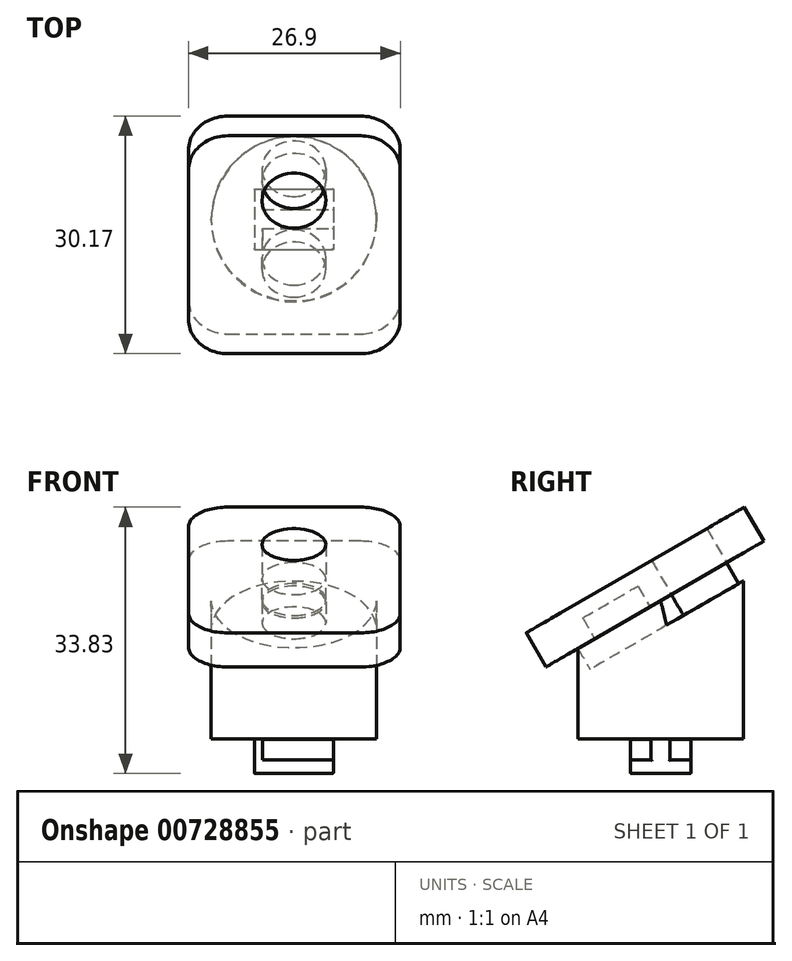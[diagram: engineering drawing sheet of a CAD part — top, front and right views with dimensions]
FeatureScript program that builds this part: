
annotation { "Feature Type Name" : "Feature", "Feature Type Description" : "" }
export const myFeature = defineFeature(function(context is Context, id is Id, definition is map)
    precondition{}
    {
        {
            var Q0;
            Q0=qCreatedBy(makeId("Top.planeOp"),FACE);
            var sketch = newSketch(context, id + "F0", { "sketchPlane" : qUnion([Q0])});
            skLineSegment(sketch, "E0.bottom", {"start": v(-34.1, 11.14) * mm, "end": v(-24.1, 11.14) * mm});
            skLineSegment(sketch, "E0.top", {"start": v(-34.1, 3.44) * mm, "end": v(-24.1, 3.44) * mm});
            skLineSegment(sketch, "E0.left", {"start": v(-34.1, 11.14) * mm, "end": v(-34.1, 3.44) * mm});
            skLineSegment(sketch, "E0.right", {"start": v(-24.1, 11.14) * mm, "end": v(-24.1, 3.44) * mm});
            skLineSegment(sketch, "E1", {"start": v(-38.76, 7.29) * mm, "end": v(-19.78, 7.29) * mm, "construction": true});
            skPoint(sketch, "E1.startSnap0", {"position": v(-34.1, 7.29) * mm});
            skLineSegment(sketch, "E2", {"start": v(-34.1, 6.09) * mm, "end": v(-24.1, 6.09) * mm});
            skLineSegment(sketch, "E3", {"start": v(-33.1, 11.14) * mm, "end": v(-33.1, 3.44) * mm});
            skLineSegment(sketch, "E4.MirrorCS", {"start": v(-34.1, 8.49) * mm, "end": v(-24.1, 8.49) * mm});
            skLineSegment(sketch, "E5", {"start": v(-29.1, 14.12) * mm, "end": v(-29.1, 1.6) * mm, "construction": true});
            skPoint(sketch, "E5.startSnap0", {"position": v(-29.1, 11.14) * mm});
            skCircle(sketch, "E6", {"center": v(-29.1, 7.29) * mm, "radius": 10.5 * mm});
            skSolve(sketch);
        }
        {
            var Q0;
            {var subQ0=sQuery(id+"F0.wireOp",EDGE,"E0.left");var subQ1=sQuery(id+"F0.wireOp",EDGE,"E0.bottom");var subQ2=makeQuery(id+"F0.imprint","INTERSECT",VERTEX,{"derivedFrom":[subQ1,subQ0]});Q0=makeQuery(id+"F0.imprint","IMPRINT",FACE,{"disambiguationData":[TD([[makeQuery(id+"F0.imprint","IMPRINT",EDGE,{"disambiguationData":[TD([[subQ2,-1.0]])],"derivedFrom":subQ1}),-1.0]])]});}
            var Q1;
            {var subQ0=sQuery(id+"F0.wireOp",EDGE,"E2");var subQ1=sQuery(id+"F0.wireOp",EDGE,"E0.left");var subQ2=makeQuery(id+"F0.imprint","INTERSECT",VERTEX,{"derivedFrom":[subQ1,subQ0]});Q1=makeQuery(id+"F0.imprint","IMPRINT",FACE,{"disambiguationData":[TD([[makeQuery(id+"F0.imprint","IMPRINT",EDGE,{"disambiguationData":[TD([[subQ2,1.0]])],"derivedFrom":subQ1}),1.0]])]});}
            var Q2;
            {var subQ0=sQuery(id+"F0.wireOp",EDGE,"E0.right");var subQ1=sQuery(id+"F0.wireOp",EDGE,"E0.bottom");var subQ2=makeQuery(id+"F0.imprint","INTERSECT",VERTEX,{"derivedFrom":[subQ1,subQ0]});Q2=makeQuery(id+"F0.imprint","IMPRINT",FACE,{"disambiguationData":[TD([[makeQuery(id+"F0.imprint","IMPRINT",EDGE,{"disambiguationData":[TD([[subQ2,1.0]])],"derivedFrom":subQ1}),-1.0]])]});}
            var Q3;
            {var subQ0=sQuery(id+"F0.wireOp",EDGE,"E2");var subQ1=sQuery(id+"F0.wireOp",EDGE,"E0.right");var subQ2=makeQuery(id+"F0.imprint","INTERSECT",VERTEX,{"derivedFrom":[subQ1,subQ0]});Q3=makeQuery(id+"F0.imprint","IMPRINT",FACE,{"disambiguationData":[TD([[makeQuery(id+"F0.imprint","IMPRINT",EDGE,{"disambiguationData":[TD([[subQ2,1.0]])],"derivedFrom":subQ1}),-1.0]])]});}
            var Q4;
            {var subQ0=sQuery(id+"F0.wireOp",EDGE,"E0.right");var subQ1=sQuery(id+"F0.wireOp",EDGE,"E0.top");var subQ2=makeQuery(id+"F0.imprint","INTERSECT",VERTEX,{"derivedFrom":[subQ1,subQ0]});Q4=makeQuery(id+"F0.imprint","IMPRINT",FACE,{"disambiguationData":[TD([[makeQuery(id+"F0.imprint","IMPRINT",EDGE,{"disambiguationData":[TD([[subQ2,1.0]])],"derivedFrom":subQ1}),1.0]])]});}
            var Q5;
            {var subQ0=sQuery(id+"F0.wireOp",EDGE,"E0.left");var subQ1=sQuery(id+"F0.wireOp",EDGE,"E0.top");var subQ2=makeQuery(id+"F0.imprint","INTERSECT",VERTEX,{"derivedFrom":[subQ1,subQ0]});Q5=makeQuery(id+"F0.imprint","IMPRINT",FACE,{"disambiguationData":[TD([[makeQuery(id+"F0.imprint","IMPRINT",EDGE,{"disambiguationData":[TD([[subQ2,-1.0]])],"derivedFrom":subQ1}),1.0]])]});}
            extrude(context, id + "F1", {"entities" : qUnion([Q0, Q1, Q2, Q3, Q4, Q5]), "depth" : 1.7 * mm, "offsetDistance" : 25 * mm});
        }
        {
            var Q0;
            {var subQ0=sQuery(id+"F0.wireOp",EDGE,"E2");var subQ1=sQuery(id+"F0.wireOp",EDGE,"E0.right");var subQ2=makeQuery(id+"F0.imprint","INTERSECT",VERTEX,{"derivedFrom":[subQ1,subQ0]});Q0=makeQuery(id+"F0.imprint","IMPRINT",FACE,{"disambiguationData":[TD([[makeQuery(id+"F0.imprint","IMPRINT",EDGE,{"disambiguationData":[TD([[subQ2,1.0]])],"derivedFrom":subQ1}),-1.0]])]});}
            extrude(context, id + "F2", {"entities" : qUnion([Q0]), "operationType" : NewBodyOperationType.ADD, "oppositeDirection" : true, "depth" : (2.6 + 1.7) * mm, "offsetDistance" : 25 * mm});
        }
        {
            var Q0;
            Q0=makeQuery(id+"F1.opExtrude","CAP_FACE",FACE,{"disambiguationData":[OSD([sQuery(id+"F0.wireOp",EDGE,"E0.bottom"),sQuery(id+"F0.wireOp",EDGE,"E0.top"),sQuery(id+"F0.wireOp",EDGE,"E0.left"),sQuery(id+"F0.wireOp",EDGE,"E0.right")])],"isStart":true});
            extrude(context, id + "F3", {"entities" : qUnion([Q0]), "operationType" : NewBodyOperationType.ADD, "depth" : (2.6 + 1.7) * mm, "offsetDistance" : 25 * mm, "hasSecondDirection" : true, "secondDirectionOppositeDirection" : false, "secondDirectionDepth" : 2.6 * mm});
        }
        {
            var Q0;
            {var subQ0=sQuery(id+"F0.wireOp",EDGE,"E0.left");var subQ1=sQuery(id+"F0.wireOp",EDGE,"E0.bottom");var subQ2=makeQuery(id+"F0.imprint","INTERSECT",VERTEX,{"derivedFrom":[subQ1,subQ0]});Q0=makeQuery(id+"F0.imprint","IMPRINT",FACE,{"disambiguationData":[TD([[makeQuery(id+"F0.imprint","IMPRINT",EDGE,{"disambiguationData":[TD([[subQ2,-1.0]])],"derivedFrom":subQ1}),-1.0]])]});}
            var Q1;
            {var subQ0=sQuery(id+"F0.wireOp",EDGE,"E2");var subQ1=sQuery(id+"F0.wireOp",EDGE,"E0.left");var subQ2=makeQuery(id+"F0.imprint","INTERSECT",VERTEX,{"derivedFrom":[subQ1,subQ0]});Q1=makeQuery(id+"F0.imprint","IMPRINT",FACE,{"disambiguationData":[TD([[makeQuery(id+"F0.imprint","IMPRINT",EDGE,{"disambiguationData":[TD([[subQ2,1.0]])],"derivedFrom":subQ1}),1.0]])]});}
            var Q2;
            {var subQ0=sQuery(id+"F0.wireOp",EDGE,"E0.left");var subQ1=sQuery(id+"F0.wireOp",EDGE,"E0.top");var subQ2=makeQuery(id+"F0.imprint","INTERSECT",VERTEX,{"derivedFrom":[subQ1,subQ0]});Q2=makeQuery(id+"F0.imprint","IMPRINT",FACE,{"disambiguationData":[TD([[makeQuery(id+"F0.imprint","IMPRINT",EDGE,{"disambiguationData":[TD([[subQ2,-1.0]])],"derivedFrom":subQ1}),1.0]])]});}
            var Q3;
            Q3=makeQuery(id+"F3.opExtrude","CAP_FACE",FACE,{"disambiguationData":[OSD([sQuery(id+"F0.wireOp",EDGE,"E0.bottom"),sQuery(id+"F0.wireOp",EDGE,"E0.top"),sQuery(id+"F0.wireOp",EDGE,"E0.left"),sQuery(id+"F0.wireOp",EDGE,"E0.right")])],"isStart":true});
            extrude(context, id + "F4", {"entities" : qUnion([Q0, Q1, Q2]), "operationType" : NewBodyOperationType.ADD, "endBound" : BoundingType.UP_TO_SURFACE, "oppositeDirection" : true, "depth" : 25 * mm, "endBoundEntityFace" : qUnion([Q3]), "offsetDistance" : 25 * mm});
        }
        {
            var Q0;
            Q0=makeQuery(id+"F0.imprint","IMPRINT",FACE,{"disambiguationData":[TD([[makeQuery(id+"F0.imprint","IMPRINT",EDGE,{"derivedFrom":sQuery(id+"F0.wireOp",EDGE,"E6")}),1.0]])]});
            extrude(context, id + "F5", {"entities" : qUnion([Q0]), "operationType" : NewBodyOperationType.ADD, "depth" : 1.7 * mm, "offsetDistance" : 25 * mm, "hasSecondDirection" : true, "secondDirectionOppositeDirection" : false, "secondDirectionDepth" : .1 * mm});
        }
        {
            var Q0;
            {var subQ0=sQuery(id+"F0.wireOp",EDGE,"E0.right");var subQ1=sQuery(id+"F0.wireOp",EDGE,"E0.top");Q0=makeQuery(id+"F2.boolean.opBoolean","SPLIT",EDGE,{"disambiguationData":[TD([makeQuery(id+"F1.opExtrude","SWEPT_FACE",FACE,{"disambiguationData":[OSD([subQ1])]})])],"derivedFrom":makeQuery(id+"F1.opExtrude","CAP_EDGE",EDGE,{"disambiguationData":[OSD([subQ0])],"isStart":true})});}
            var Q1;
            {var subQ0=sQuery(id+"F0.wireOp",EDGE,"E0.right");var subQ1=sQuery(id+"F0.wireOp",EDGE,"E0.bottom");Q1=makeQuery(id+"F2.boolean.opBoolean","SPLIT",EDGE,{"disambiguationData":[TD([makeQuery(id+"F1.opExtrude","SWEPT_FACE",FACE,{"disambiguationData":[OSD([subQ1])]})])],"derivedFrom":makeQuery(id+"F1.opExtrude","CAP_EDGE",EDGE,{"disambiguationData":[OSD([subQ0])],"isStart":true})});}
            var Q2;
            Q2=makeQuery(id+"F2.opExtrude","SWEPT_EDGE",EDGE,{"disambiguationData":[OSD([sQuery(id+"F0.wireOp",EDGE,"E0.right"),sQuery(id+"F0.wireOp",EDGE,"E2")])]});
            var Q3;
            Q3=makeQuery(id+"F2.opExtrude","SWEPT_EDGE",EDGE,{"disambiguationData":[OSD([sQuery(id+"F0.wireOp",EDGE,"E0.right"),sQuery(id+"F0.wireOp",EDGE,"E4.MirrorCS")])]});
            var Q4;
            {var subQ0=sQuery(id+"F0.wireOp",EDGE,"E0.right");var subQ1=sQuery(id+"F0.wireOp",EDGE,"E0.bottom");Q4=makeQuery(id+"F3.opExtrude","CAP_EDGE",EDGE,{"disambiguationData":[OSD([subQ0]),TDD([makeQuery(id+"F2.boolean.opBoolean","SPLIT",EDGE,{"disambiguationData":[TD([makeQuery(id+"F1.opExtrude","SWEPT_FACE",FACE,{"disambiguationData":[OSD([subQ1])]})])],"derivedFrom":makeQuery(id+"F1.opExtrude","CAP_EDGE",EDGE,{"disambiguationData":[OSD([subQ0])],"isStart":true})})])],"isStart":true});}
            var Q5;
            {var subQ0=sQuery(id+"F0.wireOp",EDGE,"E0.right");var subQ1=sQuery(id+"F0.wireOp",EDGE,"E0.top");Q5=makeQuery(id+"F3.opExtrude","CAP_EDGE",EDGE,{"disambiguationData":[OSD([subQ0]),TDD([makeQuery(id+"F2.boolean.opBoolean","SPLIT",EDGE,{"disambiguationData":[TD([makeQuery(id+"F1.opExtrude","SWEPT_FACE",FACE,{"disambiguationData":[OSD([subQ1])]})])],"derivedFrom":makeQuery(id+"F1.opExtrude","CAP_EDGE",EDGE,{"disambiguationData":[OSD([subQ0])],"isStart":true})})])],"isStart":true});}
            var Q6;
            Q6=makeQuery(id+"F3.opExtrude","SWEPT_EDGE",EDGE,{"disambiguationData":[OSD([sQuery(id+"F0.wireOp",EDGE,"E0.top"),sQuery(id+"F0.wireOp",EDGE,"E0.right")])]});
            var Q7;
            {var subQ0=sQuery(id+"F0.wireOp",EDGE,"E0.right");var subQ2=sQuery(id+"F0.wireOp",EDGE,"E0.top");var subQ4=sQuery(id+"F0.wireOp",EDGE,"E0.bottom");var subQ6=makeQuery(id+"F1.opExtrude","CAP_EDGE",EDGE,{"disambiguationData":[OSD([subQ0])],"isStart":true});Q7=makeQuery(id+"F3.boolean.opBoolean","MERGE",EDGE,{"derivedFrom":[makeQuery(id+"F2.opExtrude","CAP_EDGE",EDGE,{"disambiguationData":[OSD([subQ0])],"isStart":false}),makeQuery(id+"F3.opExtrude","CAP_EDGE",EDGE,{"disambiguationData":[OSD([subQ0]),TDD([makeQuery(id+"F2.boolean.opBoolean","SPLIT",EDGE,{"disambiguationData":[TD([makeQuery(id+"F1.opExtrude","SWEPT_FACE",FACE,{"disambiguationData":[OSD([subQ4])]})])],"derivedFrom":subQ6})])],"isStart":false}),makeQuery(id+"F3.opExtrude","CAP_EDGE",EDGE,{"disambiguationData":[OSD([subQ0]),TDD([makeQuery(id+"F2.boolean.opBoolean","SPLIT",EDGE,{"disambiguationData":[TD([makeQuery(id+"F1.opExtrude","SWEPT_FACE",FACE,{"disambiguationData":[OSD([subQ2])]})])],"derivedFrom":subQ6})])],"isStart":false})]});}
            var Q8;
            Q8=makeQuery(id+"F3.opExtrude","SWEPT_EDGE",EDGE,{"disambiguationData":[OSD([sQuery(id+"F0.wireOp",EDGE,"E0.bottom"),sQuery(id+"F0.wireOp",EDGE,"E0.right")])]});
            var Q9;
            Q9=makeQuery(id+"F1.opExtrude","CAP_EDGE",EDGE,{"disambiguationData":[OSD([sQuery(id+"F0.wireOp",EDGE,"E0.top")])],"isStart":true});
            var Q10;
            Q10=makeQuery(id+"F1.opExtrude","CAP_EDGE",EDGE,{"disambiguationData":[OSD([sQuery(id+"F0.wireOp",EDGE,"E0.bottom")])],"isStart":true});
            var Q11;
            Q11=makeQuery(id+"F3.opExtrude","CAP_EDGE",EDGE,{"disambiguationData":[OSD([sQuery(id+"F0.wireOp",EDGE,"E0.top")])],"isStart":false});
            var Q12;
            Q12=makeQuery(id+"F3.opExtrude","CAP_EDGE",EDGE,{"disambiguationData":[OSD([sQuery(id+"F0.wireOp",EDGE,"E0.bottom")])],"isStart":false});
            fillet(context, id + "F6", {"entities" : qUnion([Q0, Q1, Q2, Q3, Q4, Q5, Q6, Q7, Q8, Q9, Q10, Q11, Q12]), "radius" : .1 * mm, "tangentPropagation" : true, "allowEdgeOverflow" : false});
        }
        {
            var Q0;
            {var subQ0=sQuery(id+"F0.wireOp",EDGE,"E0.right");var subQ1=sQuery(id+"F0.wireOp",EDGE,"E0.left");var subQ2=sQuery(id+"F0.wireOp",EDGE,"E0.top");var subQ3=sQuery(id+"F0.wireOp",EDGE,"E0.bottom");Q0=makeQuery(id+"F5.boolean.opBoolean","MERGE",FACE,{"derivedFrom":[makeQuery(id+"F1.opExtrude","CAP_FACE",FACE,{"disambiguationData":[OSD([subQ3,subQ2,subQ1,subQ0])],"isStart":false}),makeQuery(id+"F5.opExtrude","CAP_FACE",FACE,{"disambiguationData":[OSD([subQ3,subQ2,subQ1,subQ0,sQuery(id+"F0.wireOp",EDGE,"E6")])],"isStart":false})]});}
            var sketch = newSketch(context, id + "F7", { "sketchPlane" : qUnion([Q0])});
            skSolve(sketch);
        }
        {
            var Q0;
            Q0=makeQuery(id+"F7.imprint","IMPRINT",FACE,{"disambiguationData":[TD([[makeQuery(id+"F7.imprint","IMPRINT",EDGE,{"derivedFrom":makeQuery(id+"F5.opExtrude","CAP_EDGE",EDGE,{"disambiguationData":[OSD([sQuery(id+"F0.wireOp",EDGE,"E6")])],"isStart":false})}),1.0]])]});
            extrude(context, id + "F8", {"entities" : qUnion([Q0]), "operationType" : NewBodyOperationType.ADD, "depth" : 22 * mm, "offsetDistance" : 25 * mm});
        }
        {
            var Q0;
            Q0=qCreatedBy(makeId("Right.planeOp"),FACE);
            var sketch = newSketch(context, id + "F9", { "sketchPlane" : qUnion([Q0])});
            skLineSegment(sketch, "E7.0", {"start": v(-3.21, 23.7) * mm, "end": v(17.79, 23.7) * mm});
            skLineSegment(sketch, "E8", {"start": v(-3.21, 23.7) * mm, "end": v(-7.26, 9.24) * mm});
            skLineSegment(sketch, "E9", {"start": v(-7.26, 9.24) * mm, "end": v(17.79, 23.7) * mm});
            skLineSegment(sketch, "E10.0", {"start": v(-3.21, 0.1) * mm, "end": v(17.79, 0.1) * mm});
            skLineSegment(sketch, "E11", {"start": v(17.79, 23.7) * mm, "end": v(-1.86, 12.36) * mm});
            skSolve(sketch);
        }
        {
            var Q0;
            {var subQ0=sQuery(id+"F9.wireOp",EDGE,"E7.0");Q0=makeQuery(id+"F9.imprint","IMPRINT",FACE,{"disambiguationData":[TD([[makeQuery(id+"F9.imprint","IMPRINT",EDGE,{"derivedFrom":subQ0}),-1.0]])]});}
            extrude(context, id + "F10", {"entities" : qUnion([Q0]), "operationType" : NewBodyOperationType.REMOVE, "endBound" : BoundingType.THROUGH_ALL, "oppositeDirection" : true, "depth" : 25 * mm, "offsetDistance" : 25 * mm, "hasSecondDirection" : true, "secondDirectionOppositeDirection" : false, "secondDirectionDepth" : 25 * mm});
        }
        {
            var Q0;
            Q0=makeQuery(id+"F10.boolean.opBoolean","COPY",FACE,{"derivedFrom":makeQuery(id+"F10.opExtrude","SWEPT_FACE",FACE,{"disambiguationData":[OSD([sQuery(id+"F9.wireOp",EDGE,"E9"),sQuery(id+"F9.wireOp",EDGE,"E11")])]})});
            var sketch = newSketch(context, id + "F11", { "sketchPlane" : qUnion([Q0])});
            skEllipse(sketch, "E12.0", {"center": v(-29.1, 15.13) * mm, "majorRadius": 12.98 * mm, "minorRadius": 10.5 * mm, "majorAxis": v(0, -1)});
            skLineSegment(sketch, "E13", {"start": v(-42.05, 15.13) * mm, "end": v(-13.49, 15.13) * mm, "construction": true});
            skLineSegment(sketch, "E14", {"start": v(-29.1, 27.25) * mm, "end": v(-29.1, -3.13) * mm, "construction": true});
            skCircle(sketch, "E15", {"center": v(-29.1, 9.5) * mm, "radius": 4.05 * mm});
            skCircle(sketch, "E16.MirrorC", {"center": v(-29.1, 20.75) * mm, "radius": 4.05 * mm});
            skSolve(sketch);
        }
        {
            var Q0;
            Q0=makeQuery(id+"F11.imprint","IMPRINT",FACE,{"disambiguationData":[TD([[makeQuery(id+"F11.imprint","IMPRINT",EDGE,{"derivedFrom":sQuery(id+"F11.wireOp",EDGE,"E15")}),1.0]])]});
            var Q1;
            Q1=makeQuery(id+"F11.imprint","IMPRINT",FACE,{"disambiguationData":[TD([[makeQuery(id+"F11.imprint","IMPRINT",EDGE,{"derivedFrom":sQuery(id+"F11.wireOp",EDGE,"E16.MirrorC")}),-1.0]])]});
            extrude(context, id + "F12", {"entities" : qUnion([Q0, Q1]), "operationType" : NewBodyOperationType.REMOVE, "oppositeDirection" : true, "depth" : 3.07 * mm, "offsetDistance" : 25 * mm});
        }
        {
            var Q0;
            Q0=makeQuery(id+"F11.imprint","IMPRINT",FACE,{"disambiguationData":[TD([[makeQuery(id+"F11.imprint","IMPRINT",EDGE,{"derivedFrom":sQuery(id+"F11.wireOp",EDGE,"E12.0")}),1.0]])]});
            var sketch = newSketch(context, id + "F13", { "sketchPlane" : qUnion([Q0])});
            skCircle(sketch, "E17.0", {"center": v(-29.1, 9.5) * mm, "radius": 4.05 * mm});
            skCircle(sketch, "E17.1", {"center": v(-29.1, 20.75) * mm, "radius": 4.05 * mm});
            skLineSegment(sketch, "E18.0", {"start": v(-42.05, 15.13) * mm, "end": v(-13.49, 15.13) * mm, "construction": true});
            skLineSegment(sketch, "E18.1", {"start": v(-29.1, 27.25) * mm, "end": v(-29.1, -3.13) * mm, "construction": true});
            skLineSegment(sketch, "E19", {"start": v(-39.5, 1.3) * mm, "end": v(-18.6, 1.3) * mm});
            skPoint(sketch, "E19.startSnap0", {"position": v(-29, 1.3) * mm});
            skPoint(sketch, "E19.startSnap1", {"position": v(-39.5, 14.28) * mm});
            skPoint(sketch, "E19.endSnap0", {"position": v(-18.6, 15.34) * mm});
            skLineSegment(sketch, "E20", {"start": v(-18.6, 1.3) * mm, "end": v(-18.6, 27.25) * mm});
            skLineSegment(sketch, "E21", {"start": v(-18.6, 27.25) * mm, "end": v(-39.5, 27.25) * mm});
            skLineSegment(sketch, "E22", {"start": v(-39.5, 27.25) * mm, "end": v(-39.5, 1.3) * mm});
            skLineSegment(sketch, "E23.0", {"start": v(-15.6, -1.7) * mm, "end": v(-15.6, 30.25) * mm});
            skLineSegment(sketch, "E23.1", {"start": v(-42.5, -1.7) * mm, "end": v(-15.6, -1.7) * mm});
            skLineSegment(sketch, "E23.2", {"start": v(-42.5, 30.25) * mm, "end": v(-42.5, -1.7) * mm});
            skLineSegment(sketch, "E23.3", {"start": v(-15.6, 30.25) * mm, "end": v(-42.5, 30.25) * mm});
            skSolve(sketch);
        }
        {
            var Q0;
            {var subQ0=sQuery(id+"F13.wireOp",EDGE,"E20");var subQ1=sQuery(id+"F13.wireOp",EDGE,"E19");var subQ2=makeQuery(id+"F13.imprint","INTERSECT",VERTEX,{"derivedFrom":[subQ1,subQ0]});Q0=makeQuery(id+"F13.imprint","IMPRINT",FACE,{"disambiguationData":[TD([[makeQuery(id+"F13.imprint","IMPRINT",EDGE,{"disambiguationData":[TD([[subQ2,1.0]])],"derivedFrom":subQ1}),1.0]])]});}
            var Q1;
            Q1=makeQuery(id+"F13.imprint","IMPRINT",FACE,{"disambiguationData":[TD([[makeQuery(id+"F13.imprint","IMPRINT",EDGE,{"derivedFrom":sQuery(id+"F13.wireOp",EDGE,"E23.0")}),1.0]])]});
            var Q2;
            {var subQ0=sQuery(id+"F13.wireOp",EDGE,"E21");var subQ1=sQuery(id+"F13.wireOp",EDGE,"E20");var subQ2=makeQuery(id+"F13.imprint","INTERSECT",VERTEX,{"derivedFrom":[subQ1,subQ0]});Q2=makeQuery(id+"F13.imprint","IMPRINT",FACE,{"disambiguationData":[TD([[makeQuery(id+"F13.imprint","IMPRINT",EDGE,{"disambiguationData":[TD([[subQ2,1.0]])],"derivedFrom":subQ1}),1.0]])]});}
            var Q3;
            {var subQ0=sQuery(id+"F13.wireOp",EDGE,"E22");var subQ1=sQuery(id+"F13.wireOp",EDGE,"E21");var subQ2=makeQuery(id+"F13.imprint","INTERSECT",VERTEX,{"derivedFrom":[subQ1,subQ0]});Q3=makeQuery(id+"F13.imprint","IMPRINT",FACE,{"disambiguationData":[TD([[makeQuery(id+"F13.imprint","IMPRINT",EDGE,{"disambiguationData":[TD([[subQ2,1.0]])],"derivedFrom":subQ1}),1.0]])]});}
            var Q4;
            {var subQ0=sQuery(id+"F13.wireOp",EDGE,"E22");var subQ1=sQuery(id+"F13.wireOp",EDGE,"E19");var subQ2=makeQuery(id+"F13.imprint","INTERSECT",VERTEX,{"derivedFrom":[subQ1,subQ0]});Q4=makeQuery(id+"F13.imprint","IMPRINT",FACE,{"disambiguationData":[TD([[makeQuery(id+"F13.imprint","IMPRINT",EDGE,{"disambiguationData":[TD([[subQ2,-1.0]])],"derivedFrom":subQ1}),1.0]])]});}
            extrude(context, id + "F14", {"entities" : qUnion([Q0, Q1, Q2, Q3, Q4]), "depth" : 5 * mm, "offsetDistance" : 25 * mm});
        }
        {
            var Q0;
            Q0=makeQuery(id+"F11.imprint","IMPRINT",FACE,{"disambiguationData":[TD([[makeQuery(id+"F11.imprint","IMPRINT",EDGE,{"derivedFrom":sQuery(id+"F11.wireOp",EDGE,"E12.0")}),1.0]])]});
            extrude(context, id + "F15", {"entities" : qUnion([Q0]), "operationType" : NewBodyOperationType.ADD, "depth" : 3.05 * mm, "offsetDistance" : 25 * mm});
        }
        {
            var Q0;
            Q0=makeQuery(id+"F11.imprint","IMPRINT",FACE,{"disambiguationData":[TD([[makeQuery(id+"F11.imprint","IMPRINT",EDGE,{"derivedFrom":sQuery(id+"F11.wireOp",EDGE,"E16.MirrorC")}),-1.0]])]});
            var Q1;
            Q1=makeQuery(id+"F11.imprint","IMPRINT",FACE,{"disambiguationData":[TD([[makeQuery(id+"F11.imprint","IMPRINT",EDGE,{"derivedFrom":sQuery(id+"F11.wireOp",EDGE,"E15")}),1.0]])]});
            var Q2;
            Q2=makeQuery(id+"F11.imprint","IMPRINT",FACE,{"disambiguationData":[TD([[makeQuery(id+"F11.imprint","IMPRINT",EDGE,{"derivedFrom":sQuery(id+"F11.wireOp",EDGE,"E12.0")}),1.0]])]});
            extrude(context, id + "F16", {"entities" : qUnion([Q0, Q1, Q2]), "operationType" : NewBodyOperationType.ADD, "depth" : 5 * mm, "offsetDistance" : 25 * mm, "hasSecondDirection" : true, "secondDirectionOppositeDirection" : false, "secondDirectionDepth" : 3.05 * mm});
        }
        {
            var Q0;
            Q0=makeQuery(id+"F14.opExtrude","SWEPT_EDGE",EDGE,{"disambiguationData":[OSD([sQuery(id+"F13.wireOp",EDGE,"E23.1"),sQuery(id+"F13.wireOp",EDGE,"E23.2")])]});
            var Q1;
            Q1=makeQuery(id+"F14.opExtrude","SWEPT_EDGE",EDGE,{"disambiguationData":[OSD([sQuery(id+"F13.wireOp",EDGE,"E23.2"),sQuery(id+"F13.wireOp",EDGE,"E23.3")])]});
            var Q2;
            Q2=makeQuery(id+"F14.opExtrude","SWEPT_EDGE",EDGE,{"disambiguationData":[OSD([sQuery(id+"F13.wireOp",EDGE,"E23.0"),sQuery(id+"F13.wireOp",EDGE,"E23.3")])]});
            var Q3;
            Q3=makeQuery(id+"F14.opExtrude","SWEPT_EDGE",EDGE,{"disambiguationData":[OSD([sQuery(id+"F13.wireOp",EDGE,"E23.0"),sQuery(id+"F13.wireOp",EDGE,"E23.1")])]});
            fillet(context, id + "F17", {"entities" : qUnion([Q0, Q1, Q2, Q3]), "radius" : 5 * mm, "tangentPropagation" : true, "allowEdgeOverflow" : false});
        }
    });
